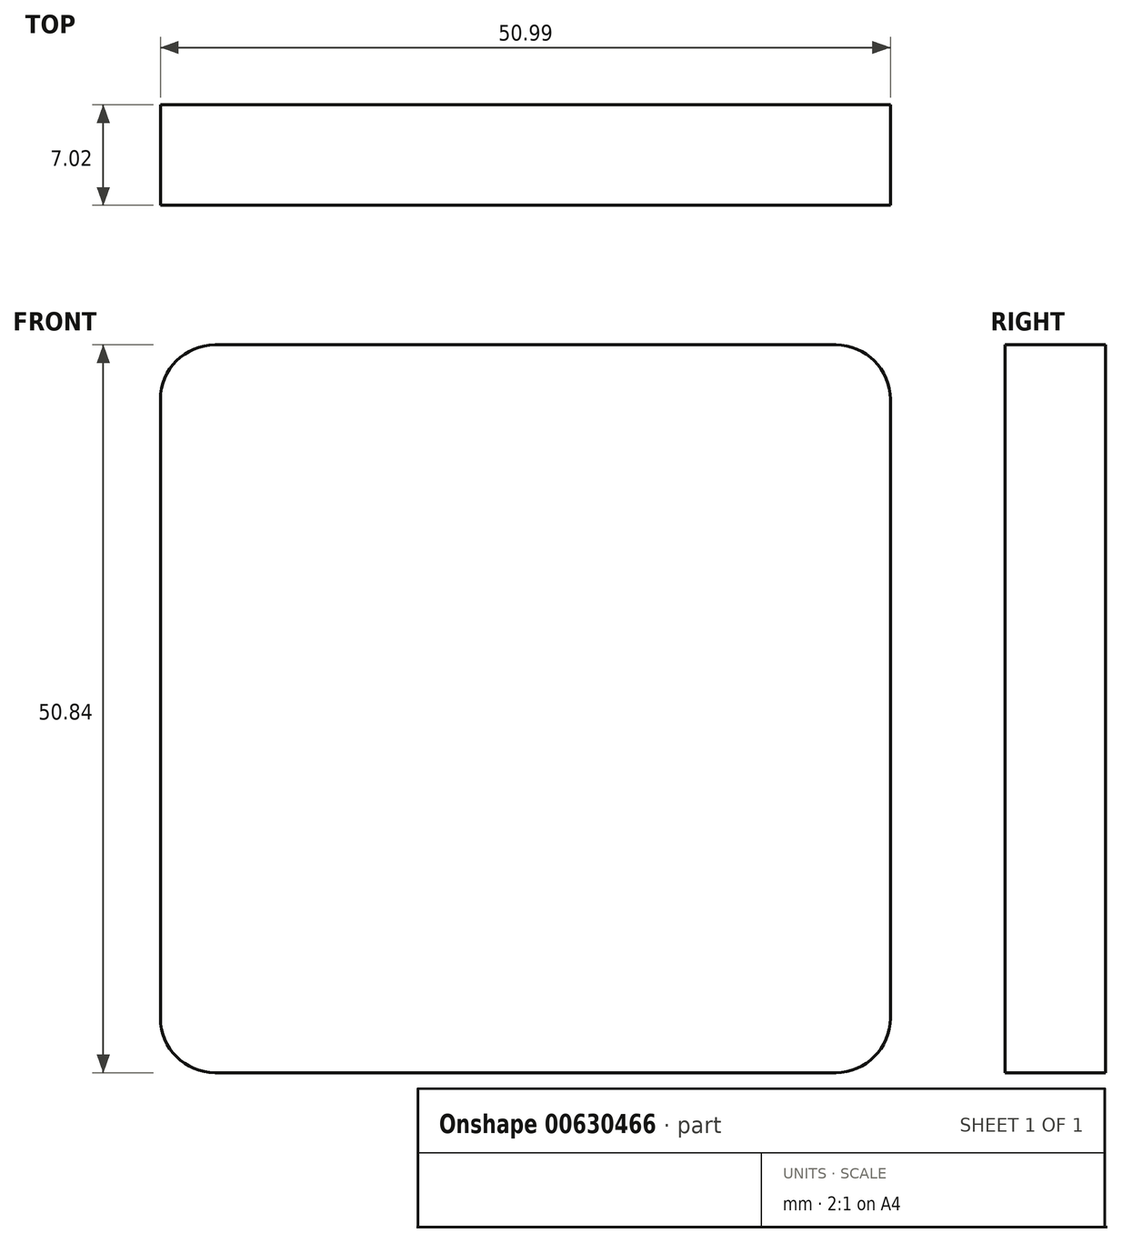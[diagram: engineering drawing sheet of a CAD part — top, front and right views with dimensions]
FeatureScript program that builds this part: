
annotation { "Feature Type Name" : "Feature", "Feature Type Description" : "" }
export const myFeature = defineFeature(function(context is Context, id is Id, definition is map)
    precondition{}
    {
        {
            var Q0;
            Q0=qCreatedBy(makeId("Front.planeOp"),FACE);
            var sketch = newSketch(context, id + "F0", { "sketchPlane" : qUnion([Q0])});
            skLineSegment(sketch, "E0.bottom", {"start": v(0, 0) * mm, "end": v(50.99, 0) * mm});
            skLineSegment(sketch, "E0.top", {"start": v(0, 50.84) * mm, "end": v(50.99, 50.84) * mm});
            skLineSegment(sketch, "E0.left", {"start": v(0, 0) * mm, "end": v(0, 50.84) * mm});
            skLineSegment(sketch, "E0.right", {"start": v(50.99, 0) * mm, "end": v(50.99, 50.84) * mm});
            skSolve(sketch);
        }
        {
            var Q0;
            Q0=makeQuery(id+"F0.imprint","IMPRINT",FACE,{"disambiguationData":[TD([[makeQuery(id+"F0.imprint","IMPRINT",EDGE,{"derivedFrom":sQuery(id+"F0.wireOp",EDGE,"E0.bottom")}),1.0]])]});
            extrude(context, id + "F1", {"entities" : qUnion([Q0]), "endBound" : BoundingType.SYMMETRIC, "depth" : 7.02 * mm, "offsetDistance" : 25.4 * mm});
        }
        {
            var Q0;
            Q0=makeQuery(id+"F1.opExtrude","SWEPT_EDGE",EDGE,{"disambiguationData":[OSD([sQuery(id+"F0.wireOp",EDGE,"E0.top"),sQuery(id+"F0.wireOp",EDGE,"E0.right")])]});
            var Q1;
            Q1=makeQuery(id+"F1.opExtrude","SWEPT_EDGE",EDGE,{"disambiguationData":[OSD([sQuery(id+"F0.wireOp",EDGE,"E0.bottom"),sQuery(id+"F0.wireOp",EDGE,"E0.right")])]});
            var Q2;
            Q2=makeQuery(id+"F1.opExtrude","SWEPT_EDGE",EDGE,{"disambiguationData":[OSD([sQuery(id+"F0.wireOp",EDGE,"E0.bottom"),sQuery(id+"F0.wireOp",EDGE,"E0.left")])]});
            var Q3;
            Q3=makeQuery(id+"F1.opExtrude","SWEPT_EDGE",EDGE,{"disambiguationData":[OSD([sQuery(id+"F0.wireOp",EDGE,"E0.top"),sQuery(id+"F0.wireOp",EDGE,"E0.left")])]});
            fillet(context, id + "F2", {"entities" : qUnion([Q0, Q1, Q2, Q3]), "radius" : 3.8 * mm, "tangentPropagation" : true, "allowEdgeOverflow" : false});
        }
    });
